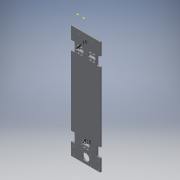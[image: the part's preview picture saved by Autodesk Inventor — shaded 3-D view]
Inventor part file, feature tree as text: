
AUTODESK INVENTOR PART (.ipt)
format: ipt  version: 2019 (Build 230136000, 136)  size: 255,488 bytes
history: native  units: in
note: dims shown in document units (in); Inventor stores cm internally (conversion verified against a paired STEP export)
features: reference x6, other x4, sketch x3, extrude x1
ambient origin geometry x8: Origin, YZ Plane, XZ Plane, XY Plane, X Axis, Y Axis, Z Axis, Center Point
bodies: Solid1 (feature_tree)
feature tree (14):
  extrude  "Extrusion1"  Depth=0.3465in
  sketch  "Sketch2"  dims[d3=3.937in]
  sketch  "Sketch3"  dims[d4=0.1969in d5=0.0in d6=0.5906in d8=0.5906in d9=2.1654in d10=2.1654in d11=0.128in d12=1.2205in d13=0.1969in d14=0.9843in d15=0.1575in d16=0.315in d17=0.1969in d18=0.0984in d19=0.1673in d20=0.1673in d21=1.8504in d22=0.4724in d23=0.1673in d24=0.1673in d25=1.063in d26=0.2756in d27=0.1673in d28=0.1673in d29=1.2598in d30=0.4724in d31=1.9685in]
  sketch  "Sketch1"  dims[d1=0.9449in d2=0.3465in]
  reference  "Reference1"
  reference  "Reference2"
  reference  "Reference3"
  reference  "Reference4"
  reference  "Reference5"
  reference  "Reference6"
  other  "<userpath>\Stuff\Ajedrez2\XCart.iam"
  other  "XCart.iam"
  other  "YPulleySupport:1"
  other  "YPulleySupportBase:1"
